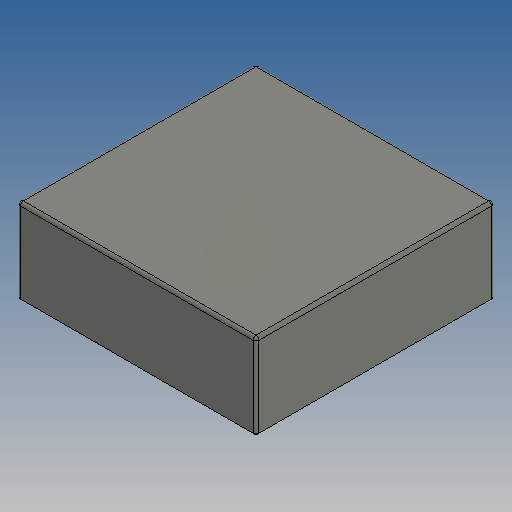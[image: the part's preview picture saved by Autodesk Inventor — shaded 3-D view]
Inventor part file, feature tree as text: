
AUTODESK INVENTOR PART (.ipt)
format: ipt  version: 2025 (Build 290162010, 162A)  size: 181,760 bytes
history: native  units: in
note: dims shown in document units (in); Inventor stores cm internally (conversion verified against a paired STEP export)
features: extrude x3, sketch x2, fillet x1, other x1
ambient origin geometry x8: Origin, YZ Plane, XZ Plane, XY Plane, X Axis, Y Axis, Z Axis, Center Point
bodies: Solid1 (feature_tree)
feature tree (7):
  extrude  "Extrusion1"  Depth=0.315in
  sketch  "Sketch3"  dims[d4=0.126in d5=0.0in d7=0.0591in d8=0.063in d11=0.063in d12=0.0in d22=0.0039in d62=0.063in d93=0.0in d95=0.0in d96=0.0in d97=0.0in d98=0.0157in d99=0.0157in d100=0.0157in d101=0.0in]
  extrude  "Extrusion2"  Depth=0.063in
  extrude  "Extrusion7"  Depth=0.063in TaperAngle=0.0deg
  fillet  "Fillet1"  Radius=0.0039in
  other  "Work Axis1"
  sketch  "Sketch2"  dims[d0=0.315in d1=0.315in]
